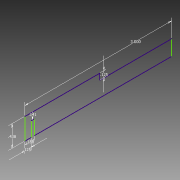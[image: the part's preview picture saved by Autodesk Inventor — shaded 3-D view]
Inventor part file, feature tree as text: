
AUTODESK INVENTOR PART (.ipt)
format: ipt  version: 2015 (Build 190159000, 159)  size: 67,072 bytes
history: native  units: in
note: dims shown in document units (in); Inventor stores cm internally (conversion verified against a paired STEP export)
features: sketch x1
ambient origin geometry x8: Origin, YZ Plane, XZ Plane, XY Plane, X Axis, Y Axis, Z Axis, Center Point
feature tree (1):
  sketch  "Sketch1"  dims[d1=3.0in d2=0.125in d3=0.1875in d4=0.1405in d5=0.125in d6=0.4375in]
